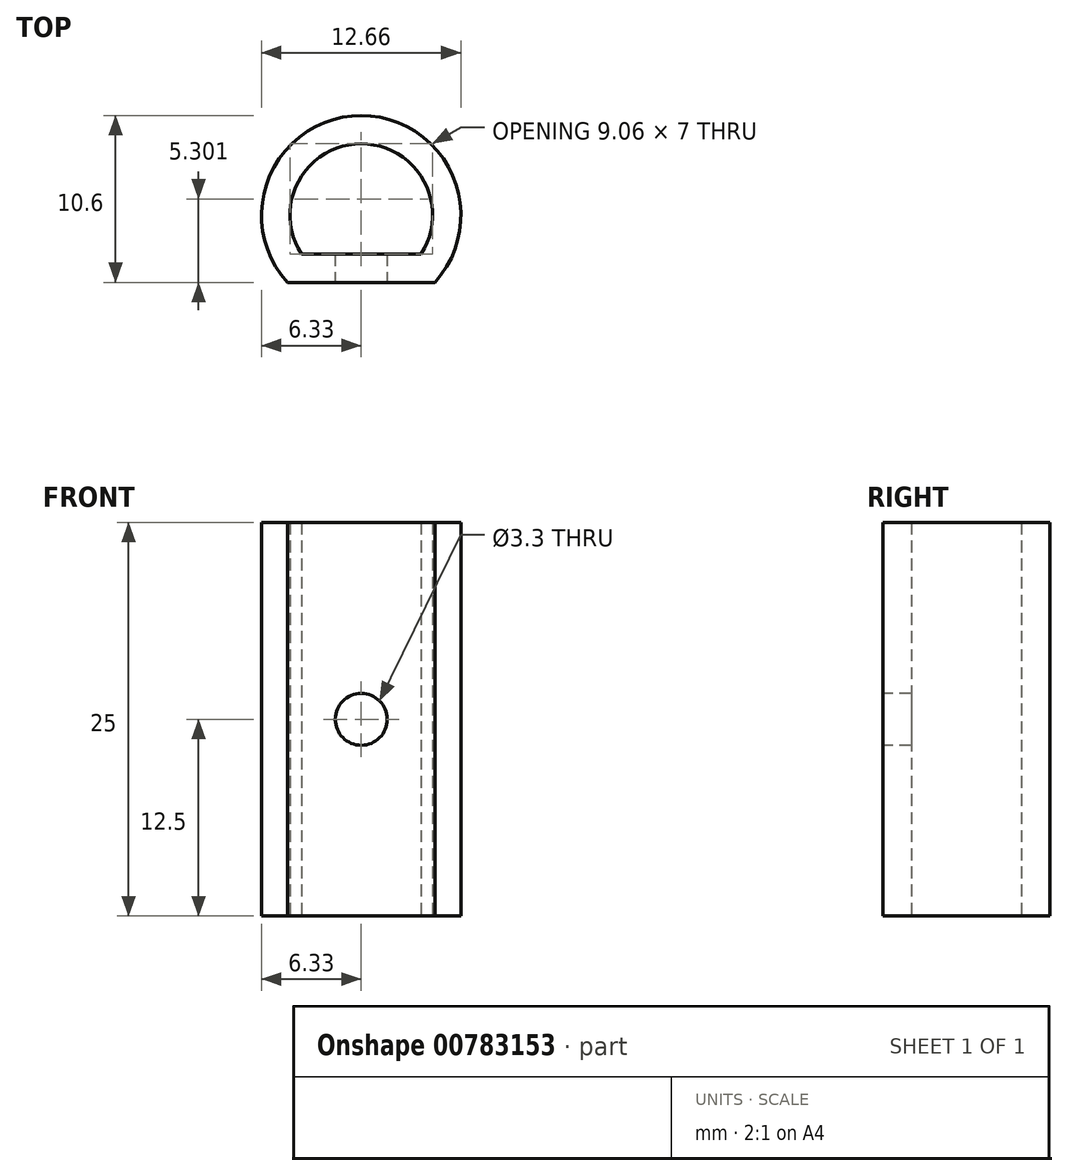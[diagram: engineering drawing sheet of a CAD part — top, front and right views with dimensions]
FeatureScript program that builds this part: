
annotation { "Feature Type Name" : "Feature", "Feature Type Description" : "" }
export const myFeature = defineFeature(function(context is Context, id is Id, definition is map)
    precondition{}
    {
        {
            var Q0;
            Q0=qCreatedBy(makeId("Top.planeOp"),FACE);
            var sketch = newSketch(context, id + "F0", { "sketchPlane" : qUnion([Q0])});
            skLineSegment(sketch, "E0", {"start": v(-3.8, 0.12) * mm, "end": v(3.8, 0.12) * mm});
            skArc(sketch, "E1", {"start": v(3.8, 0.12) * mm, "mid": v(0, 7.12) * mm, "end": v(-3.8, 0.12) * mm});
            skLineSegment(sketch, "E2", {"start": v(-2.45, 7.12) * mm, "end": v(2.15, 7.12) * mm, "construction": true});
            skArc(sketch, "E3.0", {"start": v(4.68, -1.68) * mm, "mid": v(0, 8.92) * mm, "end": v(-4.68, -1.68) * mm});
            skLineSegment(sketch, "E3.1", {"start": v(-4.68, -1.68) * mm, "end": v(4.68, -1.68) * mm});
            skLineSegment(sketch, "E4", {"start": v(-4.53, 8.91) * mm, "end": v(-4.53, -3.91) * mm, "construction": true});
            skLineSegment(sketch, "E5", {"start": v(0, -2.96) * mm, "end": v(0, 12.04) * mm, "construction": true});
            skSolve(sketch);
        }
        {
            var Q0;
            Q0=makeQuery(id+"F0.imprint","IMPRINT",FACE,{"disambiguationData":[TD([[makeQuery(id+"F0.imprint","IMPRINT",EDGE,{"derivedFrom":sQuery(id+"F0.wireOp",EDGE,"E0")}),-1.0]])]});
            extrude(context, id + "F1", {"entities" : qUnion([Q0]), "depth" : 25 * mm, "offsetDistance" : 25 * mm});
        }
        {
            var Q0;
            Q0=makeQuery(id+"F1.opExtrude","SWEPT_FACE",FACE,{"disambiguationData":[OSD([sQuery(id+"F0.wireOp",EDGE,"E3.1")])]});
            var sketch = newSketch(context, id + "F2", { "sketchPlane" : qUnion([Q0])});
            skLineSegment(sketch, "E6", {"start": v(4.68, 25) * mm, "end": v(-4.68, 0) * mm, "construction": true});
            skPoint(sketch, "E7", {"position": v(0, 12.5) * mm});
            skSolve(sketch);
        }
        {
            var Q0;
            Q0=sQuery(id+"F2.wireOp",VERTEX,"E7");
            var Q1;
            Q1=makeQuery(id+"F1.opExtrude","SWEPT_BODY",BODY,{"disambiguationData":[OSD([sQuery(id+"F0.wireOp",EDGE,"E0"),sQuery(id+"F0.wireOp",EDGE,"E1"),sQuery(id+"F0.wireOp",EDGE,"E3.0"),sQuery(id+"F0.wireOp",EDGE,"E3.1")])]});
            hole(context, id + "F3", {"style" : HoleStyle.SIMPLE, "endStyle" : HoleEndStyle.BLIND, "standardTappedOrClearance" : lookupTablePath({ "standard" : "ISO", "fit" : "Normal", "size" : "M3", "type" : "Clearance" }), "standardBlindInLast" : lookupTablePath({ "fit" : "Standard", "standard" : "ISO", "size" : "M3", "type" : "Clearance" }), "holeDiameter" : 3.3 * mm, "majorDiameter" : 5 * mm, "holeDepth" : 2 * mm, "isTappedThrough" : true, "tappedDepth" : 12 * mm, "tapClearance" : 3, "locations" : qUnion([Q0]), "scope" : qUnion([Q1])});
        }
    });
